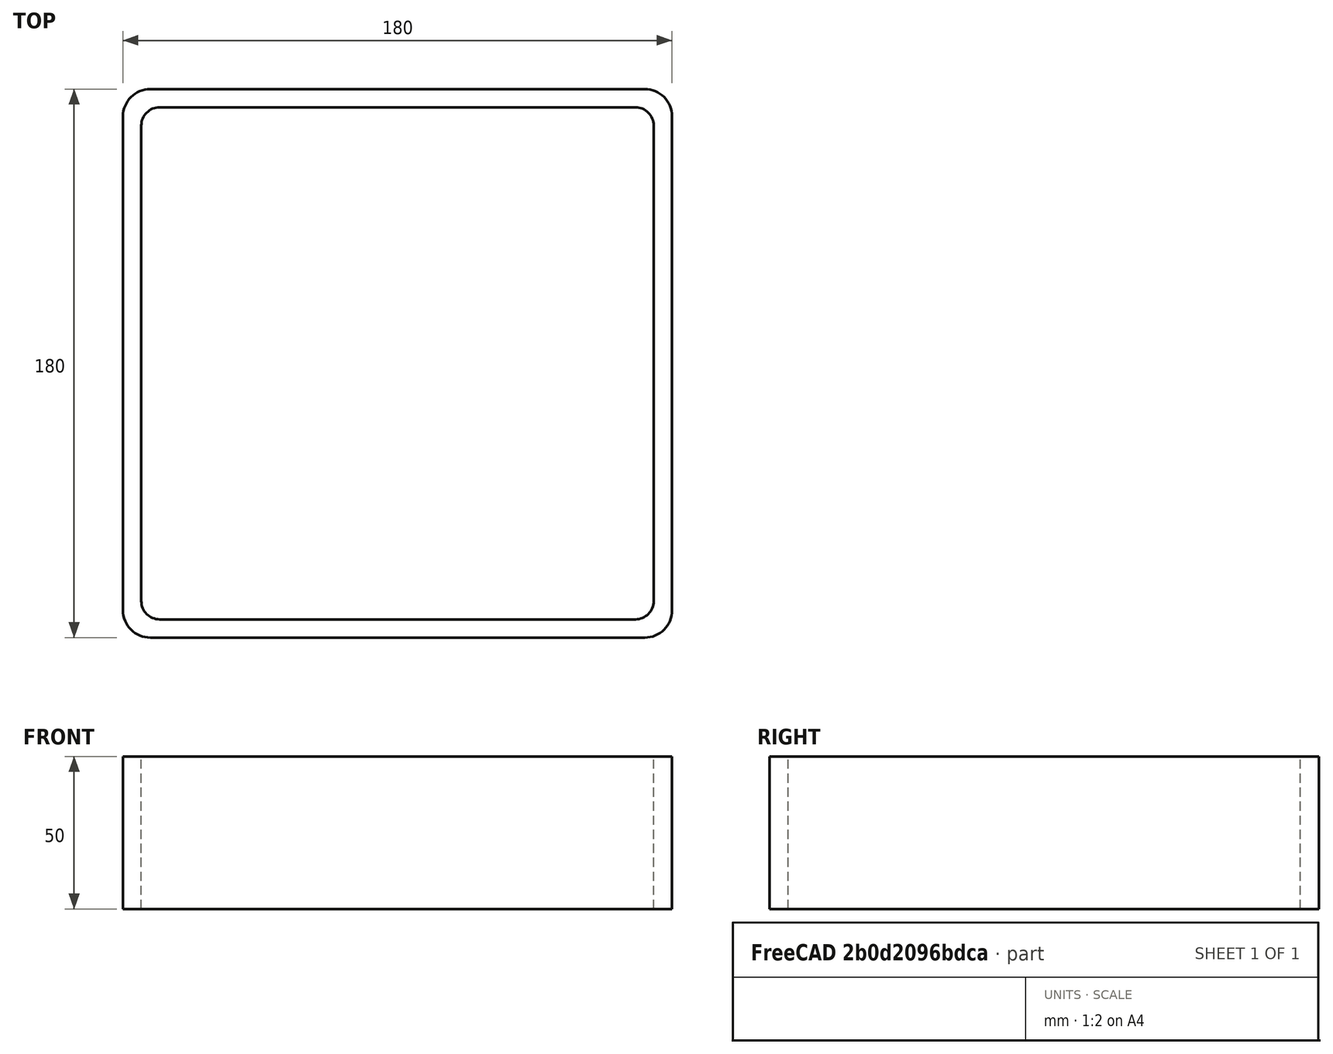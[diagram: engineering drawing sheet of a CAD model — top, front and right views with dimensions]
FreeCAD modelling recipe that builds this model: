
FCSTD DOCUMENT  (FreeCAD 0.15R4671 (Git))
Label: Square hollow section 180x180x6 EN10219 S235JRH
License: All rights reserved
LicenseURL: http://en.wikipedia.org/wiki/All_rights_reserved
objects: Sketcher::SketchObject×1, Part::Extrusion×1
note: 2 computed .brp shape members not serialized (recipe doc carries the construction recipe); baked Part::Feature solids carry a one-line shape summary decoded from their .brp

FEATURE [Sketcher::SketchObject] Sketch
  sketch-geometry (16):
    g0: LineSegment StartX=-78 StartY=84 StartZ=0 EndX=78 EndY=84 EndZ=0
    g1: LineSegment StartX=84 StartY=78 StartZ=0 EndX=84 EndY=-78 EndZ=0
    g2: LineSegment StartX=78 StartY=-84 StartZ=0 EndX=-78 EndY=-84 EndZ=0
    g3: LineSegment StartX=-84 StartY=-78 StartZ=0 EndX=-84 EndY=78 EndZ=0
    g4: LineSegment StartX=-81 StartY=90 StartZ=0 EndX=81 EndY=90 EndZ=0
    g5: LineSegment StartX=90 StartY=81 StartZ=0 EndX=90 EndY=-81 EndZ=0
    g6: LineSegment StartX=81 StartY=-90 StartZ=0 EndX=-81 EndY=-90 EndZ=0
    g7: LineSegment StartX=-90 StartY=-81 StartZ=0 EndX=-90 EndY=81 EndZ=0
    g8: ArcOfCircle CenterX=-78 CenterY=78 CenterZ=0 NormalX=0 NormalY=0 NormalZ=1 Radius=6 StartAngle=1.5708 EndAngle=3.14159
    g9: ArcOfCircle CenterX=78 CenterY=78 CenterZ=0 NormalX=0 NormalY=0 NormalZ=1 Radius=6 StartAngle=0 EndAngle=1.5708
    g10: ArcOfCircle CenterX=78 CenterY=-78 CenterZ=0 NormalX=0 NormalY=0 NormalZ=1 Radius=6 StartAngle=4.71239 EndAngle=6.28319
    g11: ArcOfCircle CenterX=-78 CenterY=-78 CenterZ=0 NormalX=0 NormalY=0 NormalZ=1 Radius=6 StartAngle=3.14159 EndAngle=4.71239
    g12: ArcOfCircle CenterX=81 CenterY=81 CenterZ=0 NormalX=0 NormalY=0 NormalZ=1 Radius=9 StartAngle=0 EndAngle=1.5708
    g13: ArcOfCircle CenterX=81 CenterY=-81 CenterZ=0 NormalX=0 NormalY=0 NormalZ=1 Radius=9 StartAngle=4.71239 EndAngle=6.28319
    g14: ArcOfCircle CenterX=-81 CenterY=-81 CenterZ=0 NormalX=0 NormalY=0 NormalZ=1 Radius=9 StartAngle=3.14159 EndAngle=4.71239
    g15: ArcOfCircle CenterX=-81 CenterY=81 CenterZ=0 NormalX=0 NormalY=0 NormalZ=1 Radius=9 StartAngle=1.5708 EndAngle=3.14159
  constraints (36):
    c: Horizontal(g2)
    c: Vertical(g3)
    c: Horizontal(g6)
    c: Vertical(g7)
    c: Tangent(g3,g8) = 1.5708
    c: Tangent(g0,g8) = 1.5708
    c: Tangent(g0,g9) = 1.5708
    c: Tangent(g1,g9) = 1.5708
    c: Tangent(g1,g10) = 1.5708
    c: Tangent(g2,g10) = 1.5708
    c: Tangent(g2,g11) = 1.5708
    c: Tangent(g3,g11) = 1.5708
    c: Tangent(g4,g12) = 1.5708
    c: Tangent(g5,g12) = 1.5708
    c: Tangent(g5,g13) = 1.5708
    c: Tangent(g6,g13) = 1.5708
    c: Tangent(g6,g14) = 1.5708
    c: Tangent(g7,g14) = 1.5708
    c: Tangent(g7,g15) = 1.5708
    c: Tangent(g4,g15) = 1.5708
    c: Equal(g9,g8)
    c: Equal(g9,g11)
    c: Equal(g9,g10)
    c: Equal(g12,g15)
    c: Equal(g12,g14)
    c: Equal(g12,g13)
    c: Symmetric(g4,g6,g-1)
    c: Symmetric(g7,g5,g-2)
    c: DistanceY(g4,g6) = -180
    c: DistanceX(g7,g5) = 180
    c: Symmetric(g3,g1,g-2)
    c: Symmetric(g0,g2,g-1)
    c: DistanceY(g0,g4) = 6
    c: DistanceX(g5,g1) = -6
    c: Radius(g9) = 6
    c: Radius(g12) = 9
FEATURE [Part::Extrusion] Extrude  label="Square hollow section 180x180x6 EN10219 S235JRH"
  Base = -> Sketch
  Dir = (0,0,50)
  Solid = true
